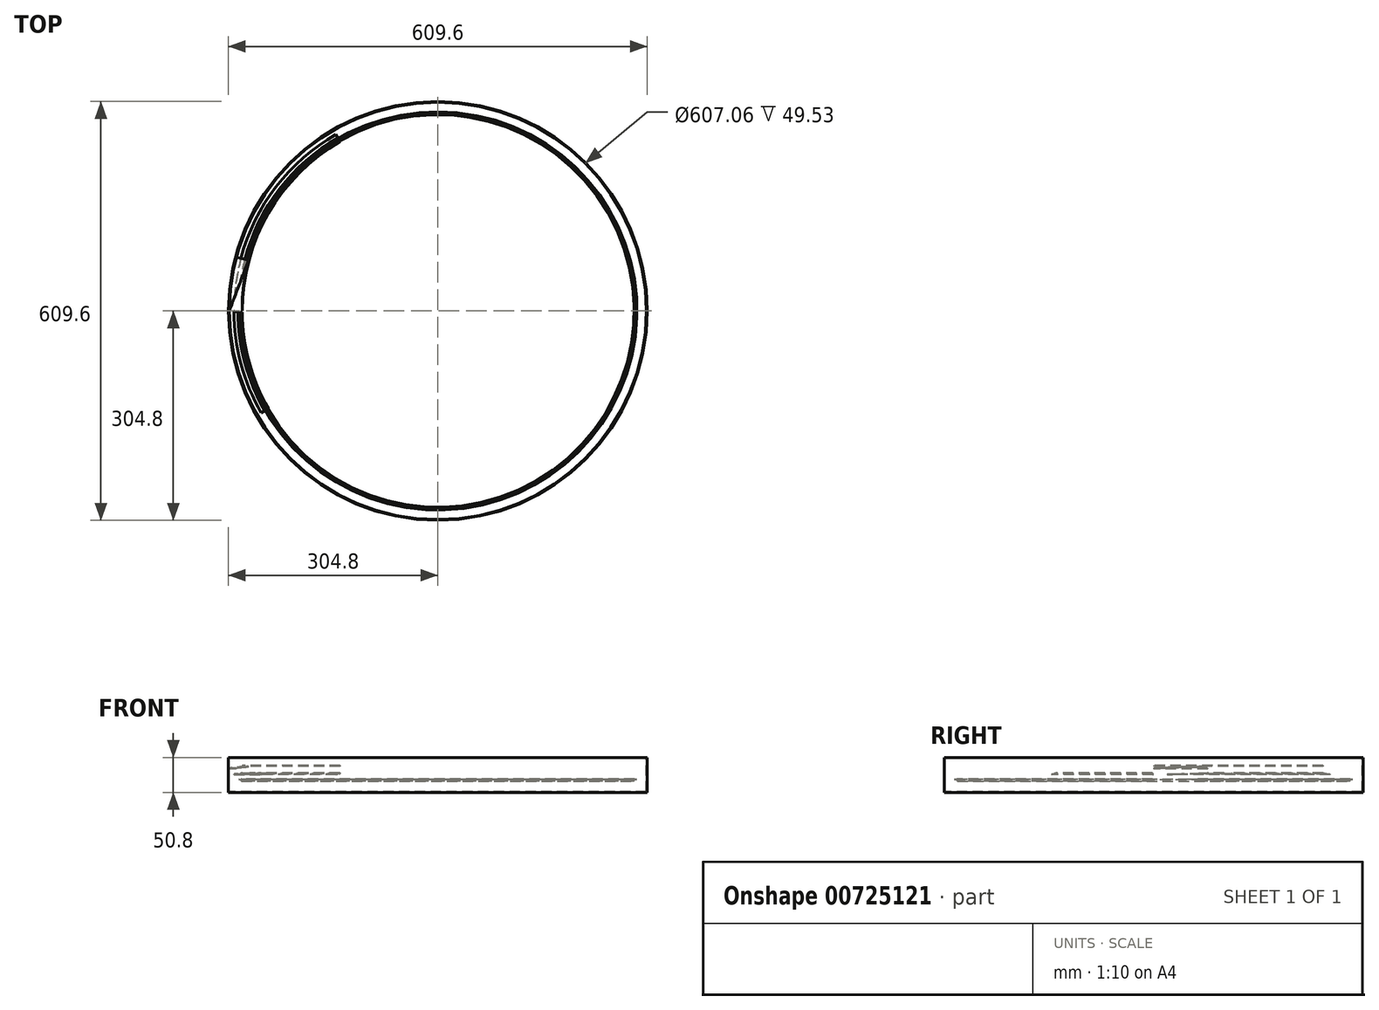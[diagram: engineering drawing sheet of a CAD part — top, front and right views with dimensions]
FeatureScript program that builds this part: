
annotation { "Feature Type Name" : "Feature", "Feature Type Description" : "" }
export const myFeature = defineFeature(function(context is Context, id is Id, definition is map)
    precondition{}
    {
        {
            var Q0;
            Q0=qCreatedBy(makeId("Front.planeOp"),FACE);
            var sketch = newSketch(context, id + "F0", { "sketchPlane" : qUnion([Q0])});
            skLineSegment(sketch, "E0.left", {"start": v(-304.8, -3.12) * mm, "end": v(-304.8, -28.52) * mm});
            skPoint(sketch, "E1.orphan", {"position": v(-304.8, 0) * mm});
            skLineSegment(sketch, "E2", {"start": v(-304.8, -3.12) * mm, "end": v(-304.8, 22.28) * mm});
            skLineSegment(sketch, "E3", {"start": v(-304.8, 22.28) * mm, "end": v(-303.53, 22.28) * mm});
            skLineSegment(sketch, "E4", {"start": v(-303.53, 22.28) * mm, "end": v(-303.53, -2.74) * mm});
            skLineSegment(sketch, "E5", {"start": v(-304.8, -28.52) * mm, "end": v(0, -28.52) * mm});
            skLineSegment(sketch, "E6", {"start": v(-303.53, -27.25) * mm, "end": v(-303.53, -4.1) * mm});
            skLineSegment(sketch, "E7", {"start": v(-303.53, -27.25) * mm, "end": v(0, -27.25) * mm});
            skLineSegment(sketch, "E8", {"start": v(0, -28.52) * mm, "end": v(0, -27.25) * mm});
            skLineSegment(sketch, "E9", {"start": v(-296.67, -1.9) * mm, "end": v(-290.83, -1.18) * mm});
            skLineSegment(sketch, "E10", {"start": v(-303.53, -2.74) * mm, "end": v(-303.53, -4.1) * mm});
            skLineSegment(sketch, "E11", {"start": v(-284.62, -0.42) * mm, "end": v(-284.62, -1.28) * mm});
            skLineSegment(sketch, "E12.trimOffspring", {"start": v(-287.3, -0.75) * mm, "end": v(-284.62, -0.42) * mm});
            skLineSegment(sketch, "E13", {"start": v(-303.53, 6.86) * mm, "end": v(-285.56, 9.07) * mm});
            skLineSegment(sketch, "E14", {"start": v(-285.56, 7.79) * mm, "end": v(-285.56, 9.07) * mm});
            skLineSegment(sketch, "E15", {"start": v(-285.56, 7.79) * mm, "end": v(-303.53, 5.58) * mm});
            skLineSegment(sketch, "E16", {"start": v(-296.67, -1.9) * mm, "end": v(-296.57, -2.75) * mm});
            skLineSegment(sketch, "E17", {"start": v(-296.57, -2.75) * mm, "end": v(-290.73, -2.03) * mm});
            skLineSegment(sketch, "E18", {"start": v(-290.83, -1.18) * mm, "end": v(-290.73, -2.03) * mm});
            skLineSegment(sketch, "E19", {"start": v(-287.3, -0.75) * mm, "end": v(-287.2, -1.6) * mm});
            skLineSegment(sketch, "E20", {"start": v(-287.2, -1.6) * mm, "end": v(-284.62, -1.28) * mm});
            skLineSegment(sketch, "E21", {"start": v(-289.8, -9.6) * mm, "end": v(-289.77, -9.84) * mm});
            skLineSegment(sketch, "E22", {"start": v(-289.8, -9.6) * mm, "end": v(-289.3, -9.53) * mm});
            skLineSegment(sketch, "E23", {"start": v(-289.3, -9.53) * mm, "end": v(-289.26, -9.78) * mm});
            skLineSegment(sketch, "E24", {"start": v(-289.26, -9.78) * mm, "end": v(-289.77, -9.84) * mm});
            skLineSegment(sketch, "E25", {"start": v(-284.83, 10.43) * mm, "end": v(-284.58, 10.46) * mm});
            skLineSegment(sketch, "E26", {"start": v(-284.83, 10.43) * mm, "end": v(-284.68, 9.17) * mm});
            skLineSegment(sketch, "E27", {"start": v(-284.68, 9.17) * mm, "end": v(-284.43, 9.2) * mm});
            skLineSegment(sketch, "E28", {"start": v(-284.58, 10.46) * mm, "end": v(-284.43, 9.2) * mm});
            skLineSegment(sketch, "E29", {"start": v(-286.27, -9.16) * mm, "end": v(-285.92, -11.98) * mm});
            skLineSegment(sketch, "E30", {"start": v(-286.27, -9.16) * mm, "end": v(-286.02, -9.13) * mm});
            skLineSegment(sketch, "E31", {"start": v(-285.88, -12.3) * mm, "end": v(-285.63, -12.28) * mm});
            skLineSegment(sketch, "E32", {"start": v(-286.02, -9.13) * mm, "end": v(-285.63, -12.28) * mm});
            skLineSegment(sketch, "E33", {"start": v(-285.92, -11.98) * mm, "end": v(-285.88, -12.3) * mm});
            skSolve(sketch);
        }
        {
            var Q0;
            Q0=qCreatedBy(makeId("Front.planeOp"),FACE);
            var sketch = newSketch(context, id + "F1", { "sketchPlane" : qUnion([Q0])});
            skLineSegment(sketch, "E34", {"start": v(0, 40.5) * mm, "end": v(0, -62.38) * mm});
            skSolve(sketch);
        }
        {
            var Q0;
            Q0=makeQuery(id+"F0.imprint","IMPRINT",FACE,{"disambiguationData":[TD([[makeQuery(id+"F0.imprint","IMPRINT",EDGE,{"derivedFrom":sQuery(id+"F0.wireOp",EDGE,"E0.left")}),1.0]])]});
            var Q1;
            Q1=sQuery(id+"F1.wireOp",EDGE,"E34");
            revolve(context, id + "F2", {"surfaceOperationType" : NewSurfaceOperationType.NEW, "entities" : qUnion([Q0]), "axis" : qUnion([Q1]), "revolveType" : RevolveType.FULL});
        }
        {
            var Q0;
            Q0=makeQuery(id+"F0.imprint","IMPRINT",FACE,{"disambiguationData":[TD([[makeQuery(id+"F0.imprint","IMPRINT",EDGE,{"derivedFrom":sQuery(id+"F0.wireOp",EDGE,"pQ6oDv7N-JJg5-aNj2-zSGn-AvQwwp5hPYC0")}),1.0]])]});
            var Q1;
            Q1=makeQuery(id+"F0.imprint","IMPRINT",FACE,{"disambiguationData":[TD([[makeQuery(id+"F0.imprint","IMPRINT",EDGE,{"derivedFrom":sQuery(id+"F0.wireOp",EDGE,"E9")}),-1.0]])]});
            var Q2;
            Q2=sQuery(id+"F1.wireOp",EDGE,"E34");
            revolve(context, id + "F3", {"surfaceOperationType" : NewSurfaceOperationType.NEW, "entities" : qUnion([Q0, Q1]), "axis" : qUnion([Q2]), "revolveType" : RevolveType.TWO_DIRECTIONS, "angle" : 60 * degree, "angleBack" : 330 * degree});
        }
        {
            var Q0;
            Q0=makeQuery(id+"F2.opRevolve","SWEPT_FACE",FACE,{"disambiguationData":[OSD([sQuery(id+"F0.wireOp",EDGE,"E7")])]});
            var sketch = newSketch(context, id + "F4", { "sketchPlane" : qUnion([Q0])});
            skLineSegment(sketch, "E35", {"start": v(-303.53, 0) * mm, "end": v(-273.66, 78.17) * mm});
            skLineSegment(sketch, "E36", {"start": v(-273.66, 78.17) * mm, "end": v(-273.66, -3.17) * mm});
            skLineSegment(sketch, "E37", {"start": v(-273.66, -3.17) * mm, "end": v(-303.53, 0) * mm});
            skSolve(sketch);
        }
        {
            var Q0;
            Q0=makeQuery(id+"F0.imprint","IMPRINT",FACE,{"disambiguationData":[TD([[makeQuery(id+"F0.imprint","IMPRINT",EDGE,{"derivedFrom":sQuery(id+"F0.wireOp",EDGE,"E11")}),-1.0]])]});
            var Q1;
            Q1=sQuery(id+"F1.wireOp",EDGE,"E34");
            revolve(context, id + "F5", {"surfaceOperationType" : NewSurfaceOperationType.NEW, "entities" : qUnion([Q0]), "axis" : qUnion([Q1]), "revolveType" : RevolveType.TWO_DIRECTIONS, "angle" : 60 * degree, "angleBack" : 330 * degree});
        }
        {
            var Q0;
            Q0=makeQuery(id+"F0.imprint","IMPRINT",FACE,{"disambiguationData":[TD([[makeQuery(id+"F0.imprint","IMPRINT",EDGE,{"derivedFrom":sQuery(id+"F0.wireOp",EDGE,"E21")}),1.0]])]});
            var Q1;
            Q1=sQuery(id+"F1.wireOp",EDGE,"E34");
            revolve(context, id + "F6", {"surfaceOperationType" : NewSurfaceOperationType.NEW, "entities" : qUnion([Q0]), "axis" : qUnion([Q1]), "revolveType" : RevolveType.FULL});
        }
        {
            var Q0;
            Q0=makeQuery(id+"F2.opRevolve","SWEPT_FACE",FACE,{"disambiguationData":[OSD([sQuery(id+"F0.wireOp",EDGE,"E7")])]});
            var sketch = newSketch(context, id + "F7", { "sketchPlane" : qUnion([Q0])});
            skLineSegment(sketch, "E38", {"start": v(-268.4, 103.42) * mm, "end": v(-263.66, 114.9) * mm});
            skLineSegment(sketch, "E39", {"start": v(-263.66, 114.9) * mm, "end": v(-259.35, 113.11) * mm});
            skLineSegment(sketch, "E40", {"start": v(-259.35, 113.11) * mm, "end": v(-263.94, 102.02) * mm});
            skLineSegment(sketch, "E41", {"start": v(-263.94, 102.02) * mm, "end": v(-268.4, 103.42) * mm});
            skSolve(sketch);
        }
        {
            var Q0;
            Q0=makeQuery(id+"F7.imprint","IMPRINT",FACE,{"disambiguationData":[TD([[makeQuery(id+"F7.imprint","IMPRINT",EDGE,{"derivedFrom":sQuery(id+"F7.wireOp",EDGE,"E38")}),-1.0]])]});
            extrude(context, id + "F8", {"entities" : qUnion([Q0]), "operationType" : NewBodyOperationType.REMOVE, "depth" : 50.8 * mm, "offsetDistance" : 25.4 * mm});
        }
        {
            var Q0;
            Q0=makeQuery(id+"F0.imprint","IMPRINT",FACE,{"disambiguationData":[TD([[makeQuery(id+"F0.imprint","IMPRINT",EDGE,{"derivedFrom":sQuery(id+"F0.wireOp",EDGE,"E25")}),-1.0]])]});
            var Q1;
            Q1=sQuery(id+"F1.wireOp",EDGE,"E34");
            revolve(context, id + "F9", {"surfaceOperationType" : NewSurfaceOperationType.NEW, "entities" : qUnion([Q0]), "axis" : qUnion([Q1]), "revolveType" : RevolveType.ONE_DIRECTION, "angle" : 60 * degree});
        }
        {
            var Q0;
            Q0=makeQuery(id+"F0.imprint","IMPRINT",FACE,{"disambiguationData":[TD([[makeQuery(id+"F0.imprint","IMPRINT",EDGE,{"derivedFrom":sQuery(id+"F0.wireOp",EDGE,"E29")}),1.0]])]});
            var Q1;
            Q1=sQuery(id+"F1.wireOp",EDGE,"E34");
            revolve(context, id + "F10", {"surfaceOperationType" : NewSurfaceOperationType.NEW, "entities" : qUnion([Q0]), "axis" : qUnion([Q1]), "revolveType" : RevolveType.FULL});
        }
        {
            var Q0;
            {var subQ0=sQuery(id+"F0.wireOp",EDGE,"E13");Q0=makeQuery(id+"F0.imprint","IMPRINT",FACE,{"disambiguationData":[TD([[makeQuery(id+"F0.imprint","IMPRINT",EDGE,{"derivedFrom":subQ0}),-1.0]])]});}
            var Q1;
            Q1=sQuery(id+"F1.wireOp",EDGE,"E34");
            revolve(context, id + "F11", {"operationType" : NewBodyOperationType.ADD, "surfaceOperationType" : NewSurfaceOperationType.NEW, "entities" : qUnion([Q0]), "axis" : qUnion([Q1]), "revolveType" : RevolveType.ONE_DIRECTION, "angle" : 15 * degree});
        }
        {
            var Q0;
            Q0=makeQuery(id+"F4.imprint","IMPRINT",FACE,{"disambiguationData":[TD([[makeQuery(id+"F4.imprint","IMPRINT",EDGE,{"derivedFrom":sQuery(id+"F4.wireOp",EDGE,"E35")}),-1.0]])]});
            var Q1;
            Q1=makeQuery(id+"F11.opRevolve","SWEPT_FACE",FACE,{"disambiguationData":[OSD([sQuery(id+"F0.wireOp",EDGE,"E13")])]});
            extrude(context, id + "F12", {"entities" : qUnion([Q0]), "operationType" : NewBodyOperationType.REMOVE, "endBound" : BoundingType.UP_TO_SURFACE, "depth" : 25.4 * mm, "endBoundEntityFace" : qUnion([Q1]), "offsetDistance" : 25.4 * mm});
        }
    });
